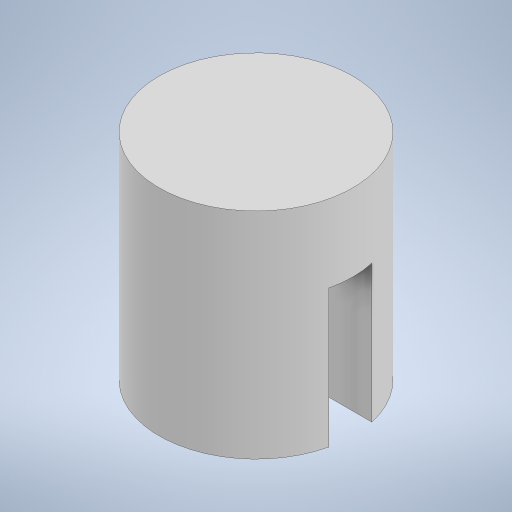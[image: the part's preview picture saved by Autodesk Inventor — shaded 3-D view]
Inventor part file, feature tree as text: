
AUTODESK INVENTOR PART (.ipt)
format: ipt  version: 2023 (Build 270158000, 158)  size: 223,232 bytes
history: native  units: in
note: dims shown in document units (in); Inventor stores cm internally (conversion verified against a paired STEP export)
features: extrude x2, sketch x1
ambient origin geometry x8: Origin, YZ Plane, XZ Plane, XY Plane, X Axis, Y Axis, Z Axis, Center Point
bodies: Solid1 (feature_tree)
feature tree (3):
  sketch  "Sketch1"  dims[d1=0.1406in d2=0.1875in d3=0.0156in d4=0.0312in d5=0.156in d6=0.0in d7=0.1in d8=0.0in]
  extrude  "Extrusion1"  Depth=0.1in
  extrude  "Extrusion2"  Depth=0.1in
